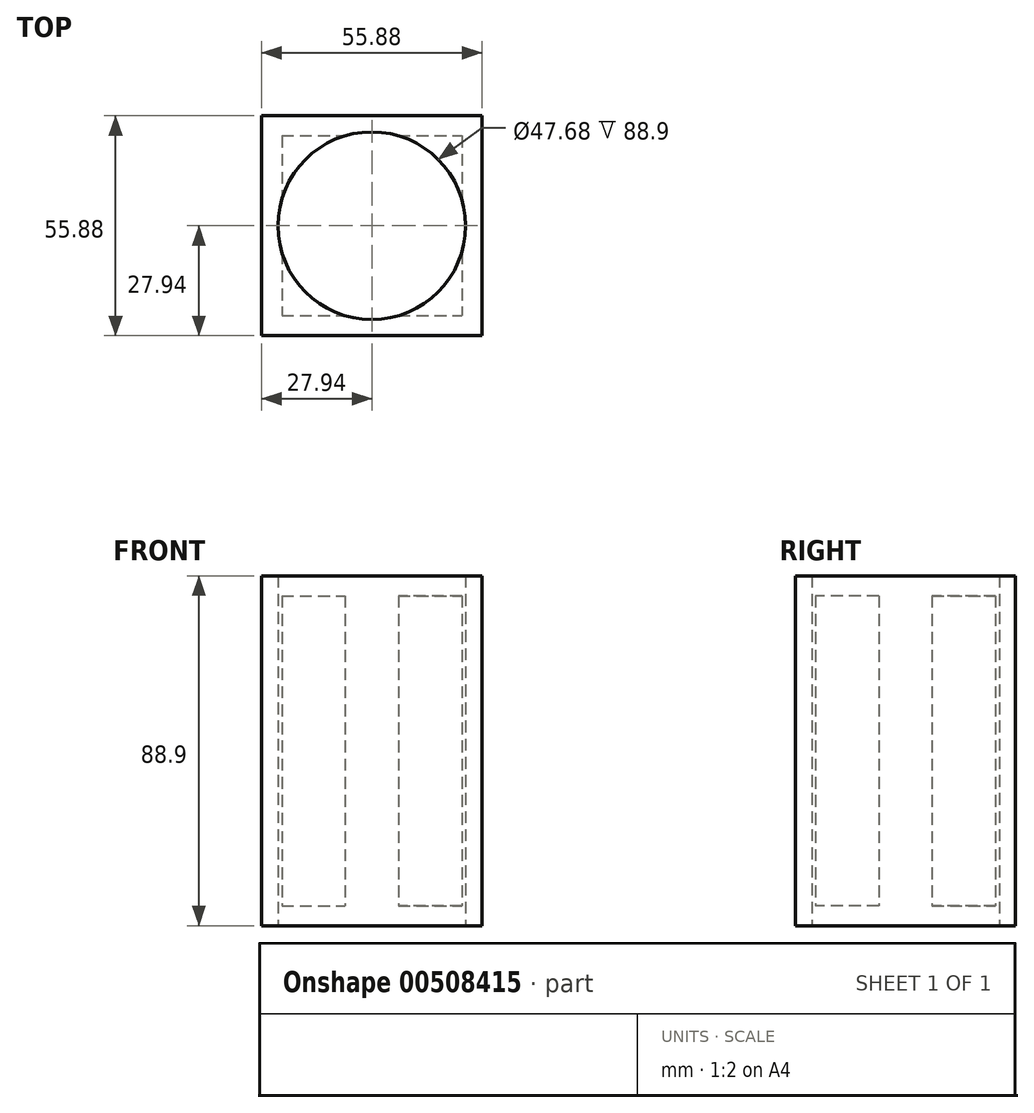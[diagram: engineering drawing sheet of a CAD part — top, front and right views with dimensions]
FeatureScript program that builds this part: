
annotation { "Feature Type Name" : "Feature", "Feature Type Description" : "" }
export const myFeature = defineFeature(function(context is Context, id is Id, definition is map)
    precondition{}
    {
        {
            var Q0;
            Q0=qCreatedBy(makeId("Top.planeOp"),FACE);
            var sketch = newSketch(context, id + "F0", { "sketchPlane" : qUnion([Q0])});
            skLineSegment(sketch, "E0.bottom", {"start": v(-27.94, 27.94) * mm, "end": v(27.94, 27.94) * mm});
            skLineSegment(sketch, "E0.top", {"start": v(-27.94, -27.94) * mm, "end": v(27.94, -27.94) * mm});
            skLineSegment(sketch, "E0.left", {"start": v(-27.94, 27.94) * mm, "end": v(-27.94, -27.94) * mm});
            skLineSegment(sketch, "E0.right", {"start": v(27.94, 27.94) * mm, "end": v(27.94, -27.94) * mm});
            skPoint(sketch, "E0.middle", {"position": v(0, 0) * mm});
            skSolve(sketch);
        }
        {
            var Q0;
            Q0 = qSketchRegion(id + "F0", true);
            extrude(context, id + "F1", {"entities" : qUnion([Q0]), "depth" : 88.9 * mm, "offsetDistance" : 25.4 * mm});
        }
        {
            var Q0;
            Q0=makeQuery(id+"F1.opExtrude","SWEPT_FACE",FACE,{"disambiguationData":[OSD([sQuery(id+"F0.wireOp",EDGE,"E0.right")])]});
            var Q1;
            Q1=makeQuery(id+"F1.opExtrude","SWEPT_BODY",BODY,{"disambiguationData":[OSD([sQuery(id+"F0.wireOp",EDGE,"E0.bottom"),sQuery(id+"F0.wireOp",EDGE,"E0.top"),sQuery(id+"F0.wireOp",EDGE,"E0.left"),sQuery(id+"F0.wireOp",EDGE,"E0.right")])]});
            shell(context, id + "F2", {"isHollow" : true, "entities" : qUnion([Q0]), "parts" : qUnion([Q1]), "thickness" : 5.08 * mm});
        }
        {
            var Q0;
            Q0=qCreatedBy(makeId("Top.planeOp"),FACE);
            var sketch = newSketch(context, id + "F3", { "sketchPlane" : qUnion([Q0])});
            skCircle(sketch, "E1", {"center": v(0, 0) * mm, "radius": 23.84 * mm});
            skSolve(sketch);
        }
        {
            var Q0;
            Q0 = qSketchRegion(id + "F3", true);
            extrude(context, id + "F4", {"entities" : qUnion([Q0]), "operationType" : NewBodyOperationType.REMOVE, "depth" : 88.9 * mm, "offsetDistance" : 25.4 * mm});
        }
    });
